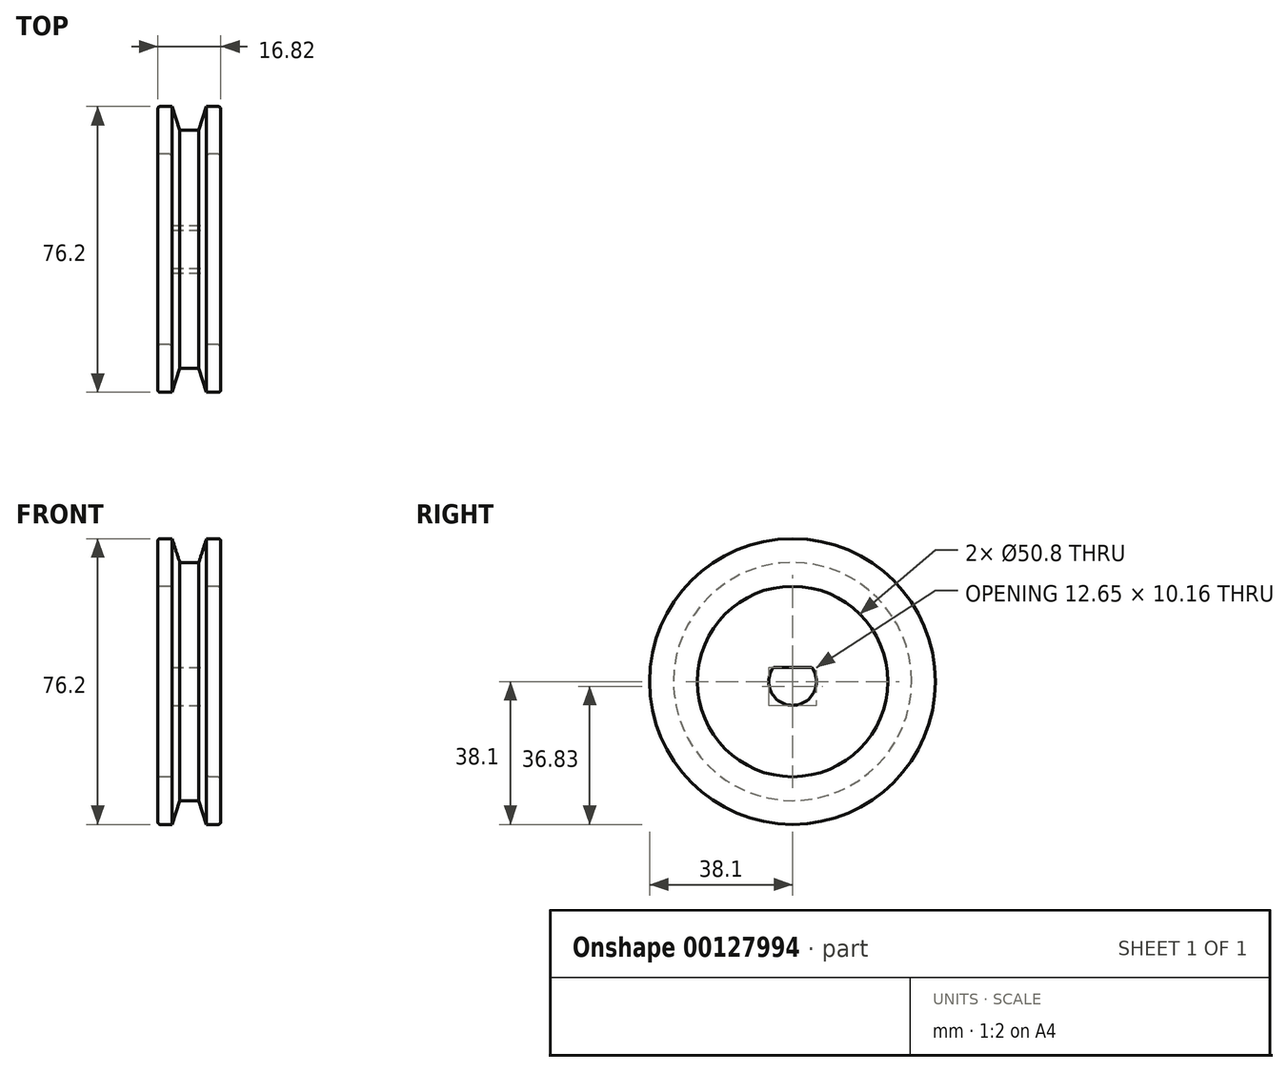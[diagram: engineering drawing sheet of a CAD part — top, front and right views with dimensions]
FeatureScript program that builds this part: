
annotation { "Feature Type Name" : "Feature", "Feature Type Description" : "" }
export const myFeature = defineFeature(function(context is Context, id is Id, definition is map)
    precondition{}
    {
        {
            var Q0;
            Q0=qCreatedBy(makeId("Front.planeOp"),FACE);
            var sketch = newSketch(context, id + "F0", { "sketchPlane" : qUnion([Q0])});
            skLineSegment(sketch, "E0", {"start": v(-4.6, 0) * mm, "end": v(-4.6, 24.77) * mm});
            skLineSegment(sketch, "E1", {"start": v(-5.23, 25.4) * mm, "end": v(-7.77, 25.4) * mm});
            skLineSegment(sketch, "E2", {"start": v(-8.4, 26.04) * mm, "end": v(-8.4, 37.46) * mm});
            skLineSegment(sketch, "E3", {"start": v(-7.77, 38.1) * mm, "end": v(-4.6, 38.1) * mm});
            skLineSegment(sketch, "E4", {"start": v(-4.6, 38.1) * mm, "end": v(-2.53, 31.75) * mm});
            skLineSegment(sketch, "E5", {"start": v(-2.53, 31.75) * mm, "end": v(0, 31.75) * mm});
            skPoint(sketch, "E6.visualSharp", {"position": v(-4.6, 25.4) * mm});
            skArc(sketch, "E6.filletArc", {"start": v(-4.6, 24.77) * mm, "mid": v(-4.78, 25.21) * mm, "end": v(-5.23, 25.4) * mm});
            skPoint(sketch, "E7.visualSharp", {"position": v(-8.4, 25.4) * mm});
            skArc(sketch, "E7.filletArc", {"start": v(-8.4, 26.04) * mm, "mid": v(-8.22, 25.59) * mm, "end": v(-7.77, 25.4) * mm});
            skPoint(sketch, "E8.visualSharp", {"position": v(-8.4, 38.1) * mm});
            skArc(sketch, "E8.filletArc", {"start": v(-7.77, 38.1) * mm, "mid": v(-8.22, 37.91) * mm, "end": v(-8.4, 37.46) * mm});
            skArc(sketch, "E9.MirrorCS", {"start": v(7.77, 38.1) * mm, "mid": v(8.22, 37.91) * mm, "end": v(8.4, 37.46) * mm});
            skArc(sketch, "E10.MirrorCS", {"start": v(4.6, 24.77) * mm, "mid": v(4.78, 25.21) * mm, "end": v(5.23, 25.4) * mm});
            skArc(sketch, "E11.MirrorCS", {"start": v(8.4, 26.04) * mm, "mid": v(8.22, 25.59) * mm, "end": v(7.77, 25.4) * mm});
            skLineSegment(sketch, "E12.MirrorCS", {"start": v(5.23, 25.4) * mm, "end": v(7.77, 25.4) * mm});
            skLineSegment(sketch, "E13.MirrorCS", {"start": v(7.77, 38.1) * mm, "end": v(4.6, 38.1) * mm});
            skPoint(sketch, "E14.MirrorP", {"position": v(8.4, 38.1) * mm});
            skPoint(sketch, "E15.MirrorP", {"position": v(8.4, 25.4) * mm});
            skLineSegment(sketch, "E16.MirrorCS", {"start": v(4.6, 38.1) * mm, "end": v(2.53, 31.75) * mm});
            skLineSegment(sketch, "E17.MirrorCS", {"start": v(8.4, 26.04) * mm, "end": v(8.4, 37.46) * mm});
            skLineSegment(sketch, "E18.MirrorCS", {"start": v(4.6, 0) * mm, "end": v(4.6, 24.77) * mm});
            skLineSegment(sketch, "E19.MirrorCS", {"start": v(2.53, 31.75) * mm, "end": v(0, 31.75) * mm});
            skPoint(sketch, "E20.MirrorP", {"position": v(4.6, 25.4) * mm});
            skLineSegment(sketch, "E21", {"start": v(-4.6, 0) * mm, "end": v(4.6, 0) * mm});
            skSolve(sketch);
        }
        {
            var Q0;
            Q0=qCreatedBy(makeId("Front.planeOp"),FACE);
            var sketch = newSketch(context, id + "F1", { "sketchPlane" : qUnion([Q0])});
            skLineSegment(sketch, "E22", {"start": v(0, 0) * mm, "end": v(17.6, 0) * mm, "construction": true});
            skSolve(sketch);
        }
        {
            var Q0;
            Q0 = qSketchRegion(id + "F0", true);
            var Q1;
            Q1=sQuery(id+"F1.wireOp",EDGE,"E22");
            revolve(context, id + "F2", {"entities" : qUnion([Q0]), "axis" : qUnion([Q1]), "revolveType" : RevolveType.FULL});
        }
        {
            var Q0;
            Q0=makeQuery(id+"F2.opRevolve","SWEPT_FACE",FACE,{"disambiguationData":[OSD([sQuery(id+"F0.wireOp",EDGE,"E18.MirrorCS")])]});
            var sketch = newSketch(context, id + "F3", { "sketchPlane" : qUnion([Q0])});
            skArc(sketch, "E23", {"start": v(-5.08, 3.81) * mm, "mid": v(0, -6.35) * mm, "end": v(5.08, 3.8) * mm});
            skLineSegment(sketch, "E24", {"start": v(5.08, 3.81) * mm, "end": v(-5.08, 3.81) * mm});
            skSolve(sketch);
        }
        {
            var Q0;
            Q0=makeQuery(id+"F3.imprint","IMPRINT",FACE,{"disambiguationData":[TD([[makeQuery(id+"F3.imprint","IMPRINT",EDGE,{"derivedFrom":sQuery(id+"F3.wireOp",EDGE,"E23")}),1.0]])]});
            extrude(context, id + "F4", {"entities" : qUnion([Q0]), "operationType" : NewBodyOperationType.REMOVE, "endBound" : BoundingType.UP_TO_NEXT, "oppositeDirection" : true, "depth" : 25.4 * mm});
        }
    });
